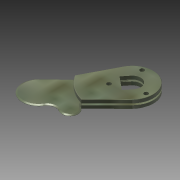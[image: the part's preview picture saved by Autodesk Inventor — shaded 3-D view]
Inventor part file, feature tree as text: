
AUTODESK INVENTOR PART (.ipt)
format: ipt  version: 2015 (Build 190159000, 159)  size: 259,584 bytes
history: native  units: mm
features: extrude x4, sketch x4, chamfer x2, fillet x2, pattern_linear x1
ambient origin geometry x8: Origin, YZ Plane, XZ Plane, XY Plane, X Axis, Y Axis, Z Axis, Center Point
bodies: 实体1 (feature_tree)
feature tree (13):
  extrude  "拉伸1"  Depth=50.0mm
  chamfer  "倒角1"  Distance=10.0mm
  chamfer  "倒角2"  Distance=10.0mm
  fillet  "圆角1"  Radius=10.0mm
  extrude  "拉伸2"  Depth=2.0mm TaperAngle=0.0deg
  pattern_linear  "矩形阵列1"  Spacing1=2.0mm  [1 undecoded]
  fillet  "圆角2"  Radius=2.0mm
  extrude  "拉伸4"  Depth=10.0mm
  extrude  "拉伸5"  Depth=10.0mm
  sketch  "草图1"  dims[d0=50.0mm d11=8.734096mm]
  sketch  "草图2"  dims[d12=8.427637mm]
  sketch  "草图4"  dims[d13=100.0mm]
  sketch  "草图5"  dims[d14=20.0mm d15=10.0mm d16=10.0mm d17=10.0mm d19=2.0mm d20=0.0mm d21=2.0mm d22=1.0mm d23=45.0deg d24=1.0mm d25=2.0mm d26=45.0deg d27=0.25mm d28=100.0mm d29=50.0mm d30=4.0mm d31=0.0mm d32=20.0mm d34=6.0mm d38=0.5mm d39=20.0mm d40=5.0mm d41=10.0mm d42=0.0mm d43=5.0mm d44=5.0mm d48=40.0mm d49=5.0mm d50=5.0mm d51=5.0mm d52=120.0deg d53=120.0deg d54=12.0mm d55=0.0mm]
note: 1 required parameter value undecoded (feature->parameter linkage not recoverable at this tier; creation-order binding heuristic only, values carry confidence <= 0.55)
